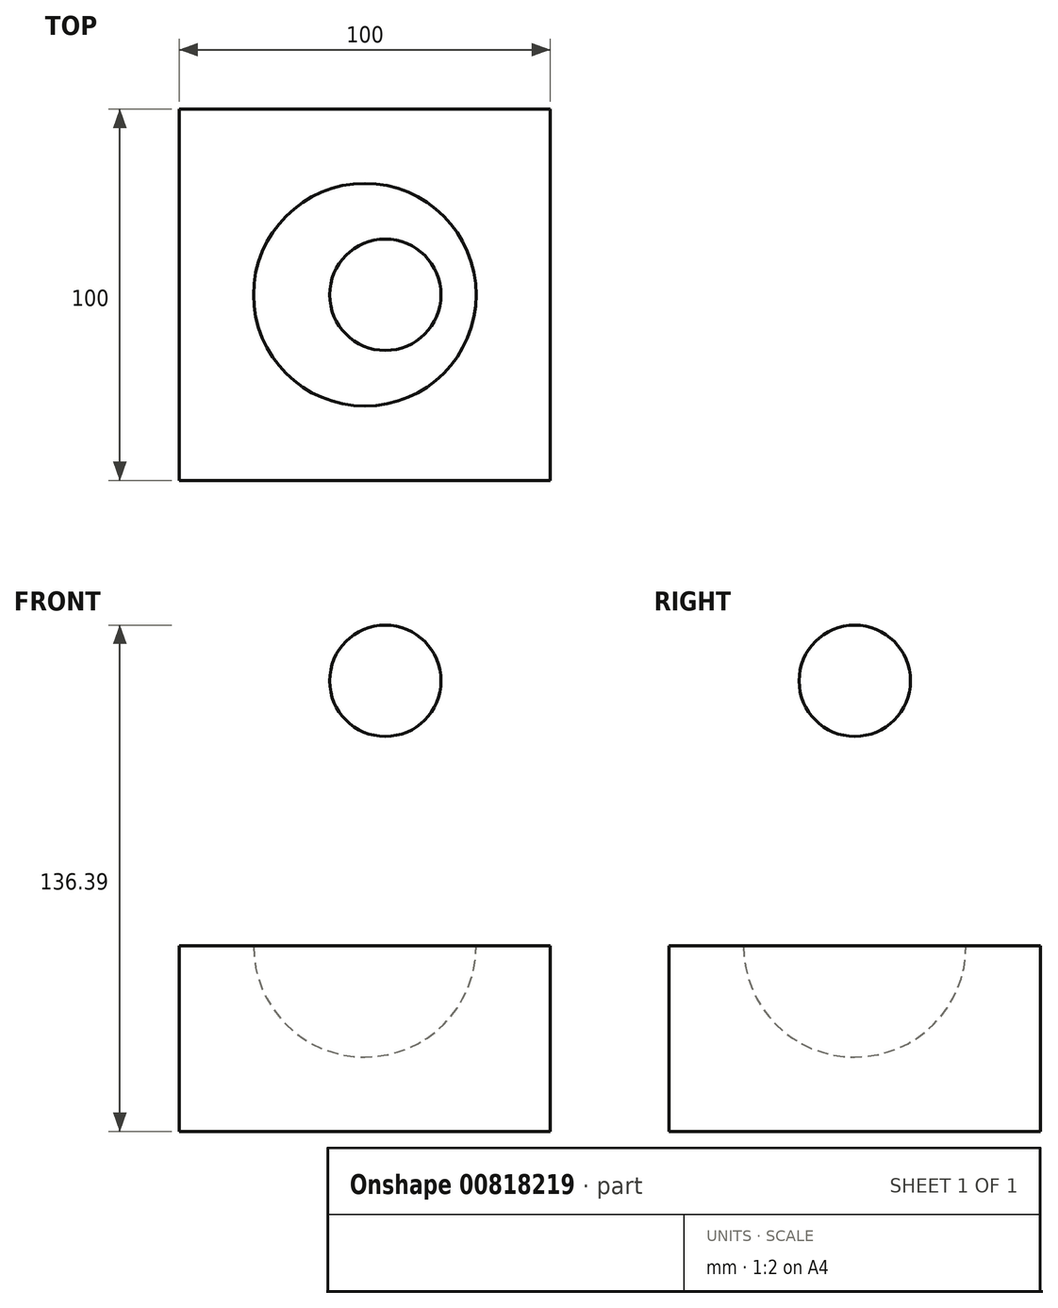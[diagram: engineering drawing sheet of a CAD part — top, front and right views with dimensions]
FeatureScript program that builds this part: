
annotation { "Feature Type Name" : "Feature", "Feature Type Description" : "" }
export const myFeature = defineFeature(function(context is Context, id is Id, definition is map)
    precondition{}
    {
        {
            var Q0;
            Q0=qCreatedBy(makeId("Top.planeOp"),FACE);
            var sketch = newSketch(context, id + "F0", { "sketchPlane" : qUnion([Q0])});
            skLineSegment(sketch, "E0.bottom", {"start": v(0, 50) * mm, "end": v(-100, 50) * mm});
            skLineSegment(sketch, "E0.top", {"start": v(0, -50) * mm, "end": v(-100, -50) * mm});
            skLineSegment(sketch, "E0.left", {"start": v(0, 50) * mm, "end": v(0, -50) * mm});
            skLineSegment(sketch, "E0.right", {"start": v(-100, 50) * mm, "end": v(-100, -50) * mm});
            skSolve(sketch);
        }
        {
            var Q0;
            Q0=makeQuery(id+"F0.imprint","IMPRINT",FACE,{"disambiguationData":[TD([[makeQuery(id+"F0.imprint","IMPRINT",EDGE,{"derivedFrom":sQuery(id+"F0.wireOp",EDGE,"E0.bottom")}),1.0]])]});
            extrude(context, id + "F1", {"entities" : qUnion([Q0]), "depth" : 50 * mm, "offsetDistance" : 25 * mm});
        }
        {
            var Q0;
            Q0=qCreatedBy(makeId("Front.planeOp"),FACE);
            var sketch = newSketch(context, id + "F2", { "sketchPlane" : qUnion([Q0])});
            skArc(sketch, "E1", {"start": v(-80, 50) * mm, "mid": v(-50, 20) * mm, "end": v(-20, 50) * mm});
            skLineSegment(sketch, "E2", {"start": v(-80, 50) * mm, "end": v(-20, 50) * mm});
            skSolve(sketch);
        }
        {
            var Q0;
            Q0 = qSketchRegion(id + "F2", true);
            var Q1;
            Q1=sQuery(id+"F2.wireOp",EDGE,"E2");
            revolve(context, id + "F3", {"operationType" : NewBodyOperationType.REMOVE, "surfaceOperationType" : NewSurfaceOperationType.NEW, "entities" : qUnion([Q0]), "axis" : qUnion([Q1]), "revolveType" : RevolveType.FULL, "oppositeDirection" : true});
        }
        {
            var Q0;
            Q0=makeQuery(id+"F1.opExtrude","CAP_FACE",FACE,{"disambiguationData":[OSD([sQuery(id+"F0.wireOp",EDGE,"E0.bottom"),sQuery(id+"F0.wireOp",EDGE,"E0.top"),sQuery(id+"F0.wireOp",EDGE,"E0.left"),sQuery(id+"F0.wireOp",EDGE,"E0.right")])],"isStart":false});
            var sketch = newSketch(context, id + "F4", { "sketchPlane" : qUnion([Q0])});
            skLineSegment(sketch, "E3.bottom", {"start": v(-100, 0) * mm, "end": v(0, 0) * mm});
            skLineSegment(sketch, "E3.top", {"start": v(-100, -50) * mm, "end": v(0, -50) * mm});
            skLineSegment(sketch, "E3.left", {"start": v(-100, 0) * mm, "end": v(-100, -50) * mm});
            skLineSegment(sketch, "E3.right", {"start": v(0, 0) * mm, "end": v(0, -50) * mm});
            skSolve(sketch);
        }
        {
            var Q0;
            Q0=qCreatedBy(makeId("Front.planeOp"),FACE);
            var sketch = newSketch(context, id + "F5", { "sketchPlane" : qUnion([Q0])});
            skArc(sketch, "E4", {"start": v(-44.47, 136.4) * mm, "mid": v(-59.47, 121.4) * mm, "end": v(-44.47, 106.4) * mm});
            skLineSegment(sketch, "E5", {"start": v(-44.47, 136.4) * mm, "end": v(-44.47, 106.4) * mm});
            skSolve(sketch);
        }
        {
            var Q0;
            Q0 = qSketchRegion(id + "F5", true);
            var Q1;
            Q1=sQuery(id+"F5.wireOp",EDGE,"E5");
            revolve(context, id + "F6", {"surfaceOperationType" : NewSurfaceOperationType.NEW, "entities" : qUnion([Q0]), "axis" : qUnion([Q1]), "revolveType" : RevolveType.FULL});
        }
    });
